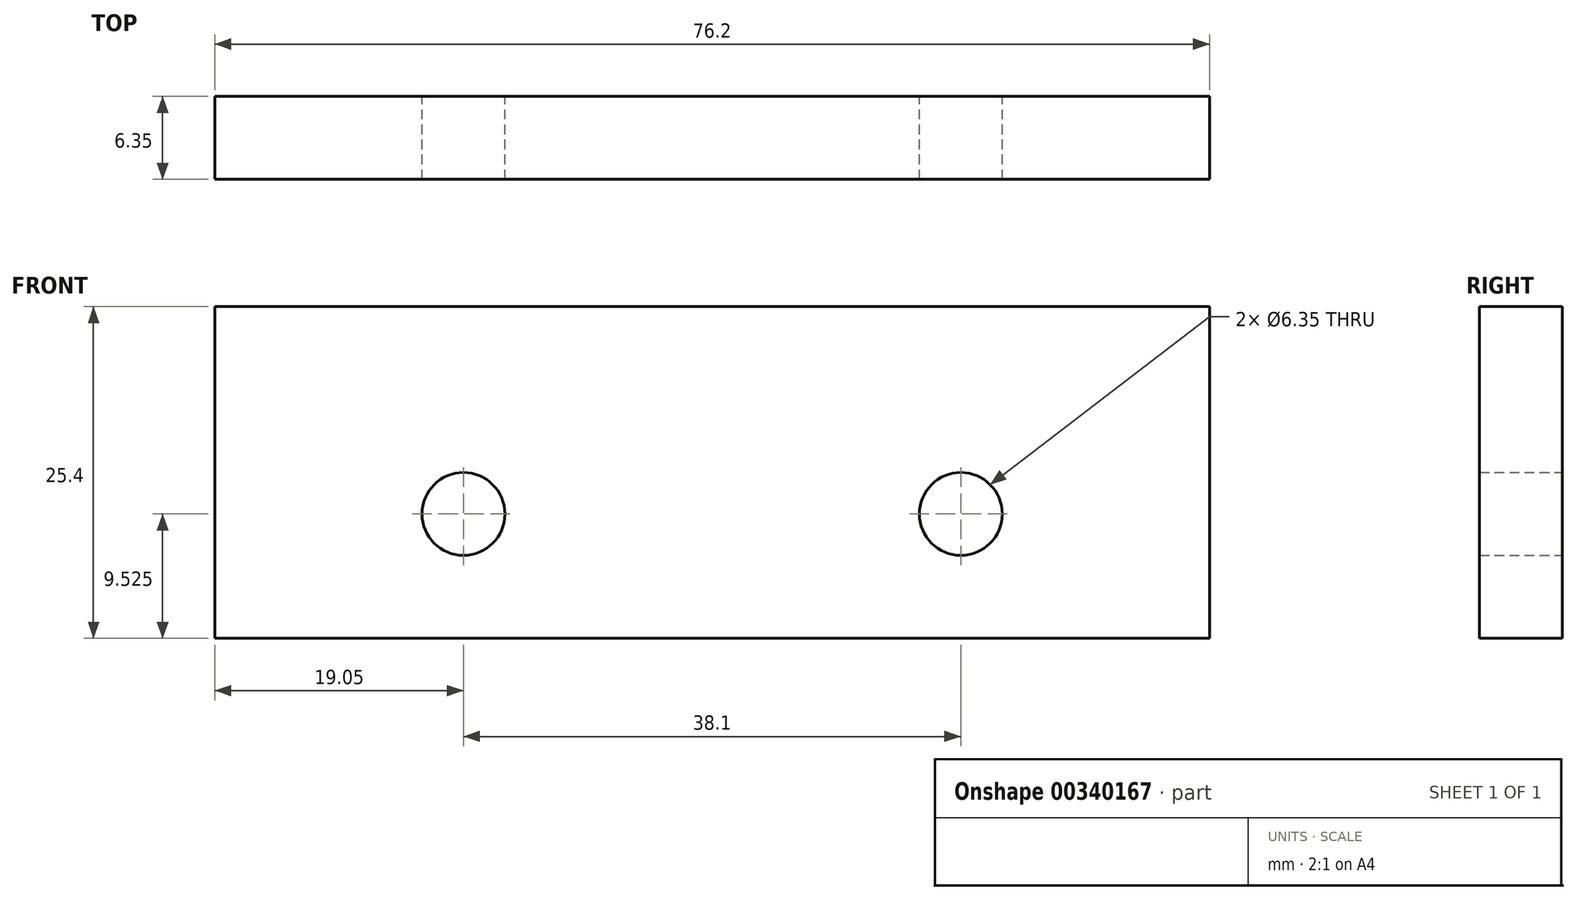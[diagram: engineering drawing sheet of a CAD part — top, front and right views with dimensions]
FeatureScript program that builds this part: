
annotation { "Feature Type Name" : "Feature", "Feature Type Description" : "" }
export const myFeature = defineFeature(function(context is Context, id is Id, definition is map)
    precondition{}
    {
        {
            var Q0;
            Q0=qCreatedBy(makeId("Front.planeOp"),FACE);
            var sketch = newSketch(context, id + "F0", { "sketchPlane" : qUnion([Q0])});
            skLineSegment(sketch, "E0.bottom", {"start": v(0, 0) * mm, "end": v(76.2, 0) * mm});
            skLineSegment(sketch, "E0.top", {"start": v(0, 25.4) * mm, "end": v(76.2, 25.4) * mm});
            skLineSegment(sketch, "E0.left", {"start": v(0, 0) * mm, "end": v(0, 25.4) * mm});
            skLineSegment(sketch, "E0.right", {"start": v(76.2, 0) * mm, "end": v(76.2, 25.4) * mm});
            skCircle(sketch, "E1", {"center": v(19.05, 9.53) * mm, "radius": 3.18 * mm});
            skCircle(sketch, "E2", {"center": v(57.15, 9.53) * mm, "radius": 3.18 * mm});
            skSolve(sketch);
        }
        {
            var Q0;
            Q0 = qSketchRegion(id + "F0", true);
            extrude(context, id + "F1", {"entities" : qUnion([Q0]), "depth" : 6.35 * mm});
        }
    });
